# Revit family: QF_ELECTROLUXPROFESSIONAL_1LSNLK_IC64825FLF_E
name_source: partatom
category: Attrezzature speciali
units: mm (PartAtom-declared; Revit-internal decimal feet)

## family parameters
Basato su piano di lavoro = No
Condiviso = No
Punto di calcolo locali = No
Quota connettore circolare = Usa diametro
Sempre verticale = Sì
Taglio con vuoti quando caricato = No
Tipo di parte = Normale

## types (3) — shared parameters
Cycle = 50 Hz
Depth Actual = 1320 mm
Height Actual = 1460 mm  [stored 4.79003 ft]
Latent Heat Output = 0.0
Length Actual = 3205 mm
Modello = IC64825FLF
Phase = 3
Produttore = Electrolux Professional
Sensible Heat Output = 0.0
URL = www.electroluxprofessional.com
Volts = 400 V
Watts = 45000 W
Weight = 1185
zero-valued in all types: Gas KW, Prospetto di default, Steam Pounds per Hour

## per-type parameters (varying)
| type | Descrizione | Item Number |
| 9882030173 | IRONER CYLINDER IC64825FLF FEEDING+LENGTH FOLDING 2540MM SUPERIOR EL. CE 400/50/3 DUBIXIUM ML VAC.FEED.TABLE ANTISTATIC | 1L0GN5 |
| 9882030300 | IRONER CYLINDER IC64825FLF FEEDING+LENGTH FOLDING 2540MM SUPERIOR EL. CE 400/50/3 DUBIXIUM FR VAC.FEED.TABLE ANTISTATIC | 1LA26W |
| 9882030247 | IRONER CYLINDER IC64825FLF FEEDING+LENGTH FOLDING 2540MM SUPERIOR EL. CE 400/50/3 DUBIXIUM SE, DK, FI VAC.FEED.TABLE ANT | 1L0GXE |

note: [stored X ft] marks values corroborated as IEEE doubles in the binary element streams (Revit-internal decimal feet)

## geometry (parser evidence)
native form markers: Sweep x13
no freeform markers — native parametric forms only
